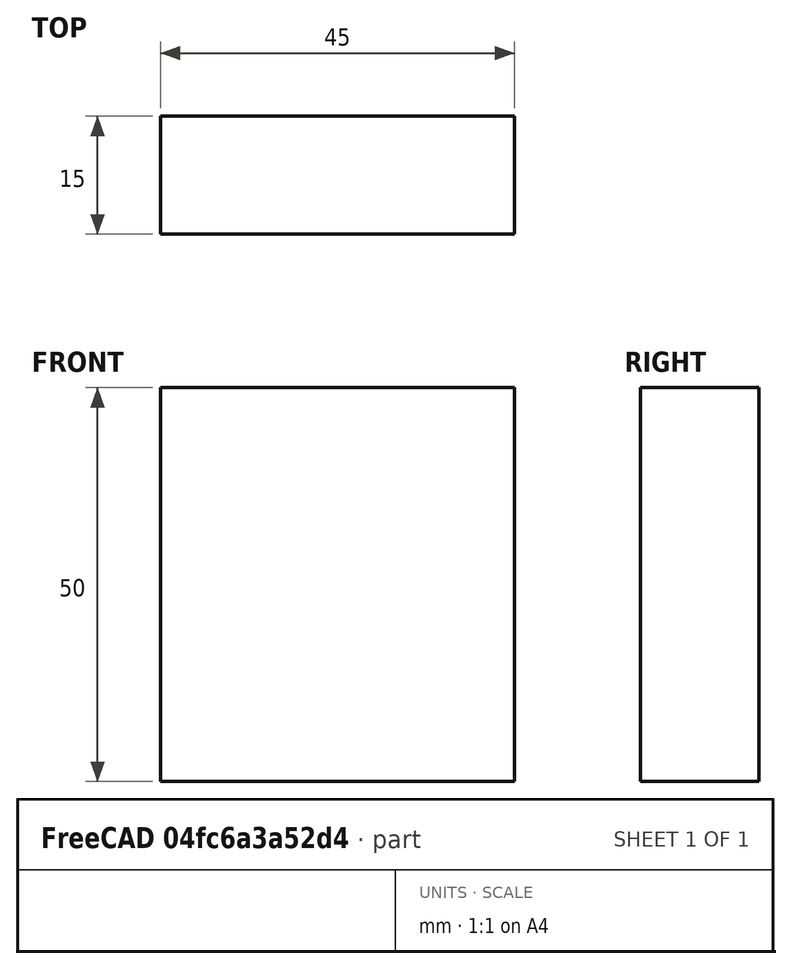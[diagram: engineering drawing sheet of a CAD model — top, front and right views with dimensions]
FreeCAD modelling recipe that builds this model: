
FCSTD DOCUMENT  (FreeCAD 0.15R4671 (Git))
Label: Flat Bar 45x15 EN10058 S235JR
License: All rights reserved
LicenseURL: http://en.wikipedia.org/wiki/All_rights_reserved
objects: Sketcher::SketchObject×1, Part::Extrusion×1
note: 2 computed .brp shape members not serialized (recipe doc carries the construction recipe); baked Part::Feature solids carry a one-line shape summary decoded from their .brp

FEATURE [Sketcher::SketchObject] Sketch
  sketch-geometry (4):
    g0: LineSegment StartX=-22.5 StartY=-7.5 StartZ=0 EndX=22.5 EndY=-7.5 EndZ=0
    g1: LineSegment StartX=22.5 StartY=-7.5 StartZ=0 EndX=22.5 EndY=7.5 EndZ=0
    g2: LineSegment StartX=22.5 StartY=7.5 StartZ=0 EndX=-22.5 EndY=7.5 EndZ=0
    g3: LineSegment StartX=-22.5 StartY=7.5 StartZ=0 EndX=-22.5 EndY=-7.5 EndZ=0
  constraints (12):
    c: Coincident(g0,g1)
    c: Coincident(g1,g2)
    c: Coincident(g2,g3)
    c: Coincident(g3,g0)
    c: Horizontal(g0)
    c: Horizontal(g2)
    c: Vertical(g1)
    c: Vertical(g3)
    c: Symmetric(g1,g2,g-2)
    c: Symmetric(g0,g1,g-1)
    c: DistanceY(g1) = 15
    c: DistanceX(g0) = 45
FEATURE [Part::Extrusion] Extrude  label="Flat Bar 45x15 EN10058 S235JR"
  Base = -> Sketch
  Dir = (0,0,50)
  Solid = true
